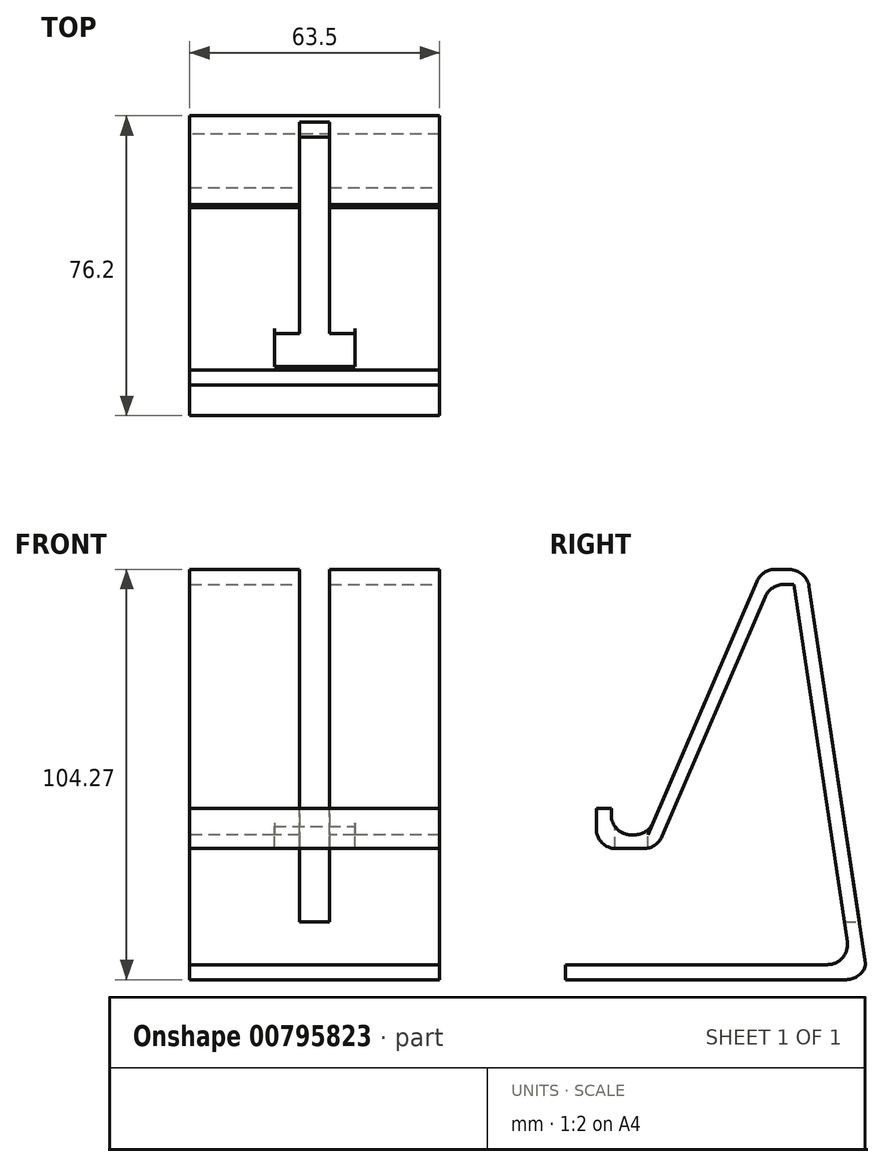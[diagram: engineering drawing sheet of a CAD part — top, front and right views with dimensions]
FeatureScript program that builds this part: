
annotation { "Feature Type Name" : "Feature", "Feature Type Description" : "" }
export const myFeature = defineFeature(function(context is Context, id is Id, definition is map)
    precondition{}
    {
        {
            var Q0;
            Q0=qCreatedBy(makeId("Top.planeOp"),FACE);
            var sketch = newSketch(context, id + "F0", { "sketchPlane" : qUnion([Q0])});
            skLineSegment(sketch, "E0.bottom", {"start": v(0, 0) * mm, "end": v(63.5, 0) * mm});
            skLineSegment(sketch, "E0.top", {"start": v(0, 76.2) * mm, "end": v(63.5, 76.2) * mm});
            skLineSegment(sketch, "E0.left", {"start": v(0, 0) * mm, "end": v(0, 76.2) * mm});
            skLineSegment(sketch, "E0.right", {"start": v(63.5, 0) * mm, "end": v(63.5, 76.2) * mm});
            skSolve(sketch);
        }
        {
            var Q0;
            Q0=makeQuery(id+"F0.imprint","IMPRINT",FACE,{"disambiguationData":[TD([[makeQuery(id+"F0.imprint","IMPRINT",EDGE,{"derivedFrom":sQuery(id+"F0.wireOp",EDGE,"E0.bottom")}),1.0]])]});
            extrude(context, id + "F1", {"entities" : qUnion([Q0]), "depth" : 3.8 * mm, "offsetDistance" : 25.4 * mm});
        }
        {
            var Q0;
            Q0=makeQuery(id+"F1.opExtrude","CAP_FACE",FACE,{"disambiguationData":[OSD([sQuery(id+"F0.wireOp",EDGE,"E0.bottom"),sQuery(id+"F0.wireOp",EDGE,"E0.top"),sQuery(id+"F0.wireOp",EDGE,"E0.left"),sQuery(id+"F0.wireOp",EDGE,"E0.right")])],"isStart":false});
            var sketch = newSketch(context, id + "F2", { "sketchPlane" : qUnion([Q0])});
            skLineSegment(sketch, "E1.bottom", {"start": v(0, 76.2) * mm, "end": v(63.5, 76.2) * mm});
            skLineSegment(sketch, "E1.top", {"start": v(0, 72.4) * mm, "end": v(63.5, 72.4) * mm});
            skLineSegment(sketch, "E1.left", {"start": v(0, 76.2) * mm, "end": v(0, 72.4) * mm});
            skLineSegment(sketch, "E1.right", {"start": v(63.5, 76.2) * mm, "end": v(63.5, 72.4) * mm});
            skSolve(sketch);
        }
        {
            var Q0;
            Q0=qCreatedBy(makeId("Right.planeOp"),FACE);
            var sketch = newSketch(context, id + "F3", { "sketchPlane" : qUnion([Q0])});
            skLineSegment(sketch, "E2", {"start": v(74.28, 3.7) * mm, "end": v(59.26, 104.18) * mm});
            skSolve(sketch);
        }
        {
            var Q0;
            Q0=makeQuery(id+"F2.imprint","IMPRINT",FACE,{"disambiguationData":[TD([[makeQuery(id+"F2.imprint","IMPRINT",EDGE,{"derivedFrom":sQuery(id+"F2.wireOp",EDGE,"E1.bottom")}),-1.0]])]});
            var Q1;
            Q1=sQuery(id+"F3.wireOp",EDGE,"E2");
            sweep(context, id + "F4", {"operationType" : NewBodyOperationType.ADD, "profiles" : qUnion([Q0]), "path" : qUnion([Q1])});
        }
        {
            var Q0;
            Q0=makeQuery(id+"F4.opSweep","SWEPT_FACE",FACE,{"disambiguationData":[OSD([sQuery(id+"F2.wireOp",EDGE,"E1.top"),sQuery(id+"F3.wireOp",EDGE,"E2")])]});
            var sketch = newSketch(context, id + "F5", { "sketchPlane" : qUnion([Q0])});
            skLineSegment(sketch, "E3.bottom", {"start": v(0, 94.55) * mm, "end": v(63.5, 94.55) * mm});
            skLineSegment(sketch, "E3.top", {"start": v(0, 90.74) * mm, "end": v(63.5, 90.74) * mm});
            skLineSegment(sketch, "E3.left", {"start": v(0, 94.55) * mm, "end": v(0, 90.74) * mm});
            skLineSegment(sketch, "E3.right", {"start": v(63.5, 94.55) * mm, "end": v(63.5, 90.74) * mm});
            skSolve(sketch);
        }
        {
            var Q0;
            Q0=qCreatedBy(makeId("Right.planeOp"),FACE);
            var sketch = newSketch(context, id + "F6", { "sketchPlane" : qUnion([Q0])});
            skLineSegment(sketch, "E4", {"start": v(57.26, 102.48) * mm, "end": v(49.73, 102.48) * mm});
            skSolve(sketch);
        }
        {
            var Q0;
            Q0=makeQuery(id+"F5.imprint","IMPRINT",FACE,{"disambiguationData":[TD([[makeQuery(id+"F5.imprint","IMPRINT",EDGE,{"derivedFrom":sQuery(id+"F5.wireOp",EDGE,"E3.bottom")}),-1.0]])]});
            var Q1;
            Q1=sQuery(id+"F6.wireOp",EDGE,"E4");
            sweep(context, id + "F7", {"operationType" : NewBodyOperationType.ADD, "profiles" : qUnion([Q0]), "path" : qUnion([Q1])});
        }
        {
            var Q0;
            Q0=makeQuery(id+"F7.boolean.opBoolean","MERGE",FACE,{"derivedFrom":[makeQuery(id+"F4.opSweep","CAP_FACE",FACE,{"disambiguationData":[OSD([sQuery(id+"F2.wireOp",EDGE,"E1.bottom"),sQuery(id+"F2.wireOp",EDGE,"E1.top"),sQuery(id+"F2.wireOp",EDGE,"E1.left"),sQuery(id+"F2.wireOp",EDGE,"E1.right"),sQuery(id+"F3.wireOp",VERTEX,"E2.end")])],"isStart":false}),makeQuery(id+"F7.opSweep","SWEPT_FACE",FACE,{"disambiguationData":[OSD([sQuery(id+"F5.wireOp",EDGE,"E3.bottom"),sQuery(id+"F6.wireOp",EDGE,"E4")])]})]});
            var sketch = newSketch(context, id + "F8", { "sketchPlane" : qUnion([Q0])});
            skLineSegment(sketch, "E5.bottom", {"start": v(0, 49.86) * mm, "end": v(63.5, 49.86) * mm});
            skLineSegment(sketch, "E5.top", {"start": v(0, 53.67) * mm, "end": v(63.5, 53.67) * mm});
            skLineSegment(sketch, "E5.left", {"start": v(0, 49.86) * mm, "end": v(0, 53.67) * mm});
            skLineSegment(sketch, "E5.right", {"start": v(63.5, 49.86) * mm, "end": v(63.5, 53.67) * mm});
            skSolve(sketch);
        }
        {
            var Q0;
            Q0=qCreatedBy(makeId("Right.planeOp"),FACE);
            var sketch = newSketch(context, id + "F9", { "sketchPlane" : qUnion([Q0])});
            skLineSegment(sketch, "E6", {"start": v(51.77, 104.28) * mm, "end": v(21.2, 33.3) * mm});
            skSolve(sketch);
        }
        {
            var Q0;
            Q0=makeQuery(id+"F8.imprint","IMPRINT",FACE,{"disambiguationData":[TD([[makeQuery(id+"F8.imprint","IMPRINT",EDGE,{"derivedFrom":sQuery(id+"F8.wireOp",EDGE,"E5.bottom")}),-1.0]])]});
            var Q1;
            Q1=sQuery(id+"F9.wireOp",EDGE,"E6");
            sweep(context, id + "F10", {"operationType" : NewBodyOperationType.ADD, "profiles" : qUnion([Q0]), "path" : qUnion([Q1])});
        }
        {
            var Q0;
            Q0=makeQuery(id+"F10.opSweep","SWEPT_FACE",FACE,{"disambiguationData":[OSD([sQuery(id+"F8.wireOp",EDGE,"E5.bottom"),sQuery(id+"F9.wireOp",EDGE,"E6")])]});
            var sketch = newSketch(context, id + "F11", { "sketchPlane" : qUnion([Q0])});
            skLineSegment(sketch, "E7.bottom", {"start": v(0, 38.23) * mm, "end": v(63.5, 38.23) * mm});
            skLineSegment(sketch, "E7.top", {"start": v(0, 42.04) * mm, "end": v(63.5, 42.04) * mm});
            skLineSegment(sketch, "E7.left", {"start": v(0, 38.23) * mm, "end": v(0, 42.04) * mm});
            skLineSegment(sketch, "E7.right", {"start": v(63.5, 38.23) * mm, "end": v(63.5, 42.04) * mm});
            skSolve(sketch);
        }
        {
            var Q0;
            Q0=qCreatedBy(makeId("Right.planeOp"),FACE);
            var sketch = newSketch(context, id + "F12", { "sketchPlane" : qUnion([Q0])});
            skLineSegment(sketch, "E8", {"start": v(21.22, 35.08) * mm, "end": v(8.52, 35.08) * mm});
            skSolve(sketch);
        }
        {
            var Q0;
            Q0=makeQuery(id+"F11.imprint","IMPRINT",FACE,{"disambiguationData":[TD([[makeQuery(id+"F11.imprint","IMPRINT",EDGE,{"derivedFrom":sQuery(id+"F11.wireOp",EDGE,"E7.bottom")}),1.0]])]});
            var Q1;
            Q1=sQuery(id+"F12.wireOp",EDGE,"E8");
            sweep(context, id + "F13", {"operationType" : NewBodyOperationType.ADD, "profiles" : qUnion([Q0]), "path" : qUnion([Q1])});
        }
        {
            var Q0;
            Q0=makeQuery(id+"F13.boolean.opBoolean","MERGE",FACE,{"derivedFrom":[makeQuery(id+"F10.opSweep","CAP_FACE",FACE,{"disambiguationData":[OSD([sQuery(id+"F8.wireOp",EDGE,"E5.bottom"),sQuery(id+"F8.wireOp",EDGE,"E5.top"),sQuery(id+"F8.wireOp",EDGE,"E5.left"),sQuery(id+"F8.wireOp",EDGE,"E5.right"),sQuery(id+"F9.wireOp",VERTEX,"E6.end")])],"isStart":true}),makeQuery(id+"F13.opSweep","SWEPT_FACE",FACE,{"disambiguationData":[OSD([sQuery(id+"F11.wireOp",EDGE,"E7.bottom"),sQuery(id+"F12.wireOp",EDGE,"E8")])]})]});
            var sketch = newSketch(context, id + "F14", { "sketchPlane" : qUnion([Q0])});
            skLineSegment(sketch, "E9.bottom", {"start": v(0, -7.75) * mm, "end": v(63.5, -7.75) * mm});
            skLineSegment(sketch, "E9.top", {"start": v(0, -11.56) * mm, "end": v(63.5, -11.56) * mm});
            skLineSegment(sketch, "E9.left", {"start": v(0, -7.75) * mm, "end": v(0, -11.56) * mm});
            skLineSegment(sketch, "E9.right", {"start": v(63.5, -7.75) * mm, "end": v(63.5, -11.56) * mm});
            skSolve(sketch);
        }
        {
            var Q0;
            Q0=makeQuery(id+"F14.imprint","IMPRINT",FACE,{"disambiguationData":[TD([[makeQuery(id+"F14.imprint","IMPRINT",EDGE,{"derivedFrom":sQuery(id+"F14.wireOp",EDGE,"E9.bottom")}),-1.0]])]});
            extrude(context, id + "F15", {"entities" : qUnion([Q0]), "operationType" : NewBodyOperationType.ADD, "oppositeDirection" : true, "depth" : 10.16 * mm, "offsetDistance" : 25.4 * mm});
        }
        {
            var Q0;
            Q0=makeQuery(id+"F13.opSweep","SWEPT_FACE",FACE,{"disambiguationData":[OSD([sQuery(id+"F11.wireOp",EDGE,"E7.top"),sQuery(id+"F12.wireOp",EDGE,"E8")])]});
            var sketch = newSketch(context, id + "F16", { "sketchPlane" : qUnion([Q0])});
            skLineSegment(sketch, "E10.bottom", {"start": v(21.52, 20.85) * mm, "end": v(41.98, 20.85) * mm});
            skLineSegment(sketch, "E10.top", {"start": v(21.52, 12.5) * mm, "end": v(41.98, 12.5) * mm});
            skLineSegment(sketch, "E10.left", {"start": v(21.52, 20.85) * mm, "end": v(21.52, 12.5) * mm});
            skLineSegment(sketch, "E10.right", {"start": v(41.98, 20.85) * mm, "end": v(41.98, 12.5) * mm});
            skPoint(sketch, "E10.middle", {"position": v(31.75, 16.68) * mm});
            skPoint(sketch, "E10.middle.positionSnap0", {"position": v(31.75, 11.56) * mm});
            skPoint(sketch, "E10.centerSnap0", {"position": v(31.75, 11.56) * mm});
            skSolve(sketch);
        }
        {
            var Q0;
            {var subQ0=sQuery(id+"F16.wireOp",EDGE,"E10.bottom");Q0=makeQuery(id+"F16.imprint","IMPRINT",FACE,{"disambiguationData":[TD([[makeQuery(id+"F16.imprint","IMPRINT",EDGE,{"derivedFrom":subQ0}),1.0]])]});}
            extrude(context, id + "F17", {"entities" : qUnion([Q0]), "operationType" : NewBodyOperationType.REMOVE, "oppositeDirection" : true, "depth" : 25.4 * mm, "offsetDistance" : 25.4 * mm});
        }
        {
            var Q0;
            Q0=makeQuery(id+"F10.opSweep","CAP_FACE",FACE,{"disambiguationData":[OSD([sQuery(id+"F8.wireOp",EDGE,"E5.bottom"),sQuery(id+"F8.wireOp",EDGE,"E5.top"),sQuery(id+"F8.wireOp",EDGE,"E5.left"),sQuery(id+"F8.wireOp",EDGE,"E5.right"),sQuery(id+"F9.wireOp",VERTEX,"E6.start")])],"isStart":false});
            var sketch = newSketch(context, id + "F18", { "sketchPlane" : qUnion([Q0])});
            skLineSegment(sketch, "E11.bottom", {"start": v(35.56, 18.16) * mm, "end": v(27.94, 18.16) * mm});
            skLineSegment(sketch, "E11.top", {"start": v(35.56, 81.66) * mm, "end": v(27.94, 81.66) * mm});
            skLineSegment(sketch, "E11.left", {"start": v(35.56, 18.16) * mm, "end": v(35.56, 81.66) * mm});
            skLineSegment(sketch, "E11.right", {"start": v(27.94, 18.16) * mm, "end": v(27.94, 81.66) * mm});
            skPoint(sketch, "E11.middle", {"position": v(31.75, 49.9) * mm});
            skSolve(sketch);
        }
        {
            var Q0;
            {var subQ0=sQuery(id+"F18.wireOp",EDGE,"E11.top");Q0=makeQuery(id+"F18.imprint","IMPRINT",FACE,{"disambiguationData":[TD([[makeQuery(id+"F18.imprint","IMPRINT",EDGE,{"derivedFrom":subQ0}),1.0]])]});}
            var Q1;
            {var subQ0=sQuery(id+"F18.wireOp",EDGE,"E11.left");var subQ1=sQuery(id+"F9.wireOp",VERTEX,"E6.start");var subQ2=makeQuery(id+"F10.opSweep","CAP_EDGE",EDGE,{"disambiguationData":[OSD([sQuery(id+"F8.wireOp",EDGE,"E5.bottom"),subQ1])],"isStart":false});var subQ3=makeQuery(id+"F18.imprint","INTERSECT",VERTEX,{"derivedFrom":[subQ2,subQ0]});Q1=makeQuery(id+"F18.imprint","IMPRINT",FACE,{"disambiguationData":[TD([[makeQuery(id+"F18.imprint","IMPRINT",EDGE,{"disambiguationData":[TD([[subQ3,-1.0]])],"derivedFrom":subQ0}),1.0]])]});}
            var Q2;
            {var subQ0=sQuery(id+"F18.wireOp",EDGE,"E11.bottom");Q2=makeQuery(id+"F18.imprint","IMPRINT",FACE,{"disambiguationData":[TD([[makeQuery(id+"F18.imprint","IMPRINT",EDGE,{"derivedFrom":subQ0}),-1.0]])]});}
            extrude(context, id + "F19", {"entities" : qUnion([Q0, Q1, Q2]), "operationType" : NewBodyOperationType.REMOVE, "oppositeDirection" : true, "depth" : 89.66 * mm, "offsetDistance" : 25.4 * mm});
        }
        {
            var Q0;
            Q0=makeQuery(id+"F15.boolean.opBoolean","MERGE",EDGE,{"derivedFrom":[makeQuery(id+"F13.opSweep","CAP_EDGE",EDGE,{"disambiguationData":[OSD([sQuery(id+"F11.wireOp",EDGE,"E7.bottom"),sQuery(id+"F12.wireOp",VERTEX,"E8.end")])],"isStart":false}),makeQuery(id+"F15.opExtrude","CAP_EDGE",EDGE,{"disambiguationData":[OSD([sQuery(id+"F14.wireOp",EDGE,"E9.bottom")])],"isStart":true})]});
            var Q1;
            {var subQ0=sQuery(id+"F9.wireOp",VERTEX,"E6.end");var subQ2=sQuery(id+"F8.wireOp",EDGE,"E5.top");Q1=makeQuery(id+"F19.boolean.opBoolean","SPLIT",EDGE,{"disambiguationData":[TD([makeQuery(id+"F1.opExtrude","SWEPT_FACE",FACE,{"disambiguationData":[OSD([sQuery(id+"F0.wireOp",EDGE,"E0.right")])]})])],"derivedFrom":makeQuery(id+"F10.opSweep","CAP_EDGE",EDGE,{"disambiguationData":[OSD([subQ2,subQ0])],"isStart":true})});}
            var Q2;
            {var subQ0=sQuery(id+"F9.wireOp",VERTEX,"E6.end");var subQ2=sQuery(id+"F8.wireOp",EDGE,"E5.top");Q2=makeQuery(id+"F19.boolean.opBoolean","SPLIT",EDGE,{"disambiguationData":[TD([makeQuery(id+"F1.opExtrude","SWEPT_FACE",FACE,{"disambiguationData":[OSD([sQuery(id+"F0.wireOp",EDGE,"E0.left")])]})])],"derivedFrom":makeQuery(id+"F10.opSweep","CAP_EDGE",EDGE,{"disambiguationData":[OSD([subQ2,subQ0])],"isStart":true})});}
            var Q3;
            {var subQ0=sQuery(id+"F9.wireOp",VERTEX,"E6.start");var subQ2=sQuery(id+"F8.wireOp",EDGE,"E5.bottom");Q3=makeQuery(id+"F19.boolean.opBoolean","SPLIT",EDGE,{"disambiguationData":[TD([makeQuery(id+"F1.opExtrude","SWEPT_FACE",FACE,{"disambiguationData":[OSD([sQuery(id+"F0.wireOp",EDGE,"E0.right")])]})])],"derivedFrom":makeQuery(id+"F10.opSweep","CAP_EDGE",EDGE,{"disambiguationData":[OSD([subQ2,subQ0])],"isStart":false})});}
            var Q4;
            {var subQ0=sQuery(id+"F9.wireOp",VERTEX,"E6.start");var subQ2=sQuery(id+"F8.wireOp",EDGE,"E5.bottom");Q4=makeQuery(id+"F19.boolean.opBoolean","SPLIT",EDGE,{"disambiguationData":[TD([makeQuery(id+"F1.opExtrude","SWEPT_FACE",FACE,{"disambiguationData":[OSD([sQuery(id+"F0.wireOp",EDGE,"E0.left")])]})])],"derivedFrom":makeQuery(id+"F10.opSweep","CAP_EDGE",EDGE,{"disambiguationData":[OSD([subQ2,subQ0])],"isStart":false})});}
            var Q5;
            {var subQ2=sQuery(id+"F2.wireOp",EDGE,"E1.bottom");var subQ4=sQuery(id+"F3.wireOp",VERTEX,"E2.end");Q5=makeQuery(id+"F19.boolean.opBoolean","SPLIT",EDGE,{"disambiguationData":[TD([makeQuery(id+"F1.opExtrude","SWEPT_FACE",FACE,{"disambiguationData":[OSD([sQuery(id+"F0.wireOp",EDGE,"E0.left")])]})])],"derivedFrom":makeQuery(id+"F4.opSweep","CAP_EDGE",EDGE,{"disambiguationData":[OSD([subQ2,subQ4])],"isStart":false})});}
            var Q6;
            {var subQ2=sQuery(id+"F2.wireOp",EDGE,"E1.bottom");var subQ3=sQuery(id+"F3.wireOp",VERTEX,"E2.end");Q6=makeQuery(id+"F19.boolean.opBoolean","SPLIT",EDGE,{"disambiguationData":[TD([makeQuery(id+"F1.opExtrude","SWEPT_FACE",FACE,{"disambiguationData":[OSD([sQuery(id+"F0.wireOp",EDGE,"E0.right")])]})])],"derivedFrom":makeQuery(id+"F4.opSweep","CAP_EDGE",EDGE,{"disambiguationData":[OSD([subQ2,subQ3])],"isStart":false})});}
            var Q7;
            {var subQ0=sQuery(id+"F9.wireOp",VERTEX,"E6.start");var subQ2=sQuery(id+"F8.wireOp",EDGE,"E5.top");Q7=makeQuery(id+"F19.boolean.opBoolean","SPLIT",EDGE,{"disambiguationData":[TD([makeQuery(id+"F1.opExtrude","SWEPT_FACE",FACE,{"disambiguationData":[OSD([sQuery(id+"F0.wireOp",EDGE,"E0.left")])]})])],"derivedFrom":makeQuery(id+"F10.opSweep","CAP_EDGE",EDGE,{"disambiguationData":[OSD([subQ2,subQ0])],"isStart":false})});}
            var Q8;
            {var subQ0=sQuery(id+"F9.wireOp",VERTEX,"E6.start");var subQ2=sQuery(id+"F8.wireOp",EDGE,"E5.top");Q8=makeQuery(id+"F19.boolean.opBoolean","SPLIT",EDGE,{"disambiguationData":[TD([makeQuery(id+"F1.opExtrude","SWEPT_FACE",FACE,{"disambiguationData":[OSD([sQuery(id+"F0.wireOp",EDGE,"E0.right")])]})])],"derivedFrom":makeQuery(id+"F10.opSweep","CAP_EDGE",EDGE,{"disambiguationData":[OSD([subQ2,subQ0])],"isStart":false})});}
            var Q9;
            {var subQ0=sQuery(id+"F6.wireOp",EDGE,"E4");var subQ1=makeQuery(id+"F7.opSweep","SWEPT_FACE",FACE,{"disambiguationData":[OSD([sQuery(id+"F5.wireOp",EDGE,"E3.top"),subQ0])]});var subQ2=sQuery(id+"F9.wireOp",EDGE,"E6");var subQ3=makeQuery(id+"F10.opSweep","SWEPT_FACE",FACE,{"disambiguationData":[OSD([sQuery(id+"F8.wireOp",EDGE,"E5.top"),subQ2])]});Q9=makeQuery(id+"F19.boolean.opBoolean","SPLIT",EDGE,{"disambiguationData":[TD([makeQuery(id+"F1.opExtrude","SWEPT_FACE",FACE,{"disambiguationData":[OSD([sQuery(id+"F0.wireOp",EDGE,"E0.right")])]})])],"derivedFrom":makeQuery(id+"F10.boolean.opBoolean","INTERSECT",EDGE,{"derivedFrom":[subQ1,subQ3]})});}
            var Q10;
            {var subQ0=sQuery(id+"F6.wireOp",EDGE,"E4");var subQ1=makeQuery(id+"F7.opSweep","SWEPT_FACE",FACE,{"disambiguationData":[OSD([sQuery(id+"F5.wireOp",EDGE,"E3.top"),subQ0])]});var subQ2=sQuery(id+"F9.wireOp",EDGE,"E6");var subQ3=makeQuery(id+"F10.opSweep","SWEPT_FACE",FACE,{"disambiguationData":[OSD([sQuery(id+"F8.wireOp",EDGE,"E5.top"),subQ2])]});Q10=makeQuery(id+"F19.boolean.opBoolean","SPLIT",EDGE,{"disambiguationData":[TD([makeQuery(id+"F1.opExtrude","SWEPT_FACE",FACE,{"disambiguationData":[OSD([sQuery(id+"F0.wireOp",EDGE,"E0.left")])]})])],"derivedFrom":makeQuery(id+"F10.boolean.opBoolean","INTERSECT",EDGE,{"derivedFrom":[subQ1,subQ3]})});}
            var Q11;
            {var subQ2=sQuery(id+"F5.wireOp",EDGE,"E3.top");Q11=makeQuery(id+"F19.boolean.opBoolean","SPLIT",EDGE,{"disambiguationData":[TD([makeQuery(id+"F1.opExtrude","SWEPT_FACE",FACE,{"disambiguationData":[OSD([sQuery(id+"F0.wireOp",EDGE,"E0.right")])]})])],"derivedFrom":makeQuery(id+"F7.opSweep","CAP_EDGE",EDGE,{"disambiguationData":[OSD([subQ2,sQuery(id+"F6.wireOp",VERTEX,"E4.start")])],"isStart":true})});}
            var Q12;
            {var subQ2=sQuery(id+"F5.wireOp",EDGE,"E3.top");Q12=makeQuery(id+"F19.boolean.opBoolean","SPLIT",EDGE,{"disambiguationData":[TD([makeQuery(id+"F1.opExtrude","SWEPT_FACE",FACE,{"disambiguationData":[OSD([sQuery(id+"F0.wireOp",EDGE,"E0.left")])]})])],"derivedFrom":makeQuery(id+"F7.opSweep","CAP_EDGE",EDGE,{"disambiguationData":[OSD([subQ2,sQuery(id+"F6.wireOp",VERTEX,"E4.start")])],"isStart":true})});}
            var Q13;
            Q13=makeQuery(id+"F1.opExtrude","CAP_EDGE",EDGE,{"disambiguationData":[OSD([sQuery(id+"F0.wireOp",EDGE,"E0.top")])],"isStart":true});
            var Q14;
            Q14=makeQuery(id+"F4.opSweep","CAP_EDGE",EDGE,{"disambiguationData":[OSD([sQuery(id+"F2.wireOp",EDGE,"E1.bottom"),sQuery(id+"F3.wireOp",VERTEX,"E2.start")])],"isStart":true});
            var Q15;
            Q15=makeQuery(id+"F4.boolean.opBoolean","INTERSECT",EDGE,{"derivedFrom":[makeQuery(id+"F1.opExtrude","CAP_FACE",FACE,{"disambiguationData":[OSD([sQuery(id+"F0.wireOp",EDGE,"E0.bottom"),sQuery(id+"F0.wireOp",EDGE,"E0.top"),sQuery(id+"F0.wireOp",EDGE,"E0.left"),sQuery(id+"F0.wireOp",EDGE,"E0.right")])],"isStart":false}),makeQuery(id+"F4.opSweep","SWEPT_FACE",FACE,{"disambiguationData":[OSD([sQuery(id+"F2.wireOp",EDGE,"E1.top"),sQuery(id+"F3.wireOp",EDGE,"E2")])]})]});
            var Q16;
            {var subQ0=sQuery(id+"F9.wireOp",EDGE,"E6");var subQ1=makeQuery(id+"F10.opSweep","SWEPT_FACE",FACE,{"disambiguationData":[OSD([sQuery(id+"F8.wireOp",EDGE,"E5.bottom"),subQ0])]});var subQ2=sQuery(id+"F12.wireOp",EDGE,"E8");var subQ3=makeQuery(id+"F13.opSweep","SWEPT_FACE",FACE,{"disambiguationData":[OSD([sQuery(id+"F11.wireOp",EDGE,"E7.top"),subQ2])]});Q16=makeQuery(id+"F17.boolean.opBoolean","SPLIT",EDGE,{"disambiguationData":[TD([makeQuery(id+"F1.opExtrude","SWEPT_FACE",FACE,{"disambiguationData":[OSD([sQuery(id+"F0.wireOp",EDGE,"E0.right")])]})])],"derivedFrom":makeQuery(id+"F13.boolean.opBoolean","INTERSECT",EDGE,{"derivedFrom":[subQ1,subQ3]})});}
            var Q17;
            {var subQ0=sQuery(id+"F9.wireOp",EDGE,"E6");var subQ1=makeQuery(id+"F10.opSweep","SWEPT_FACE",FACE,{"disambiguationData":[OSD([sQuery(id+"F8.wireOp",EDGE,"E5.bottom"),subQ0])]});var subQ2=sQuery(id+"F12.wireOp",EDGE,"E8");var subQ3=makeQuery(id+"F13.opSweep","SWEPT_FACE",FACE,{"disambiguationData":[OSD([sQuery(id+"F11.wireOp",EDGE,"E7.top"),subQ2])]});Q17=makeQuery(id+"F17.boolean.opBoolean","SPLIT",EDGE,{"disambiguationData":[TD([makeQuery(id+"F1.opExtrude","SWEPT_FACE",FACE,{"disambiguationData":[OSD([sQuery(id+"F0.wireOp",EDGE,"E0.left")])]})])],"derivedFrom":makeQuery(id+"F13.boolean.opBoolean","INTERSECT",EDGE,{"derivedFrom":[subQ1,subQ3]})});}
            var Q18;
            Q18=makeQuery(id+"F15.boolean.opBoolean","INTERSECT",EDGE,{"derivedFrom":[makeQuery(id+"F13.opSweep","SWEPT_FACE",FACE,{"disambiguationData":[OSD([sQuery(id+"F11.wireOp",EDGE,"E7.top"),sQuery(id+"F12.wireOp",EDGE,"E8")])]}),makeQuery(id+"F15.opExtrude","SWEPT_FACE",FACE,{"disambiguationData":[OSD([sQuery(id+"F14.wireOp",EDGE,"E9.top")])]})]});
            fillet(context, id + "F20", {"entities" : qUnion([Q0, Q1, Q2, Q3, Q4, Q5, Q6, Q7, Q8, Q9, Q10, Q11, Q12, Q13, Q14, Q15, Q16, Q17, Q18]), "radius" : 5.08 * mm, "tangentPropagation" : true, "allowEdgeOverflow" : false});
        }
    });
